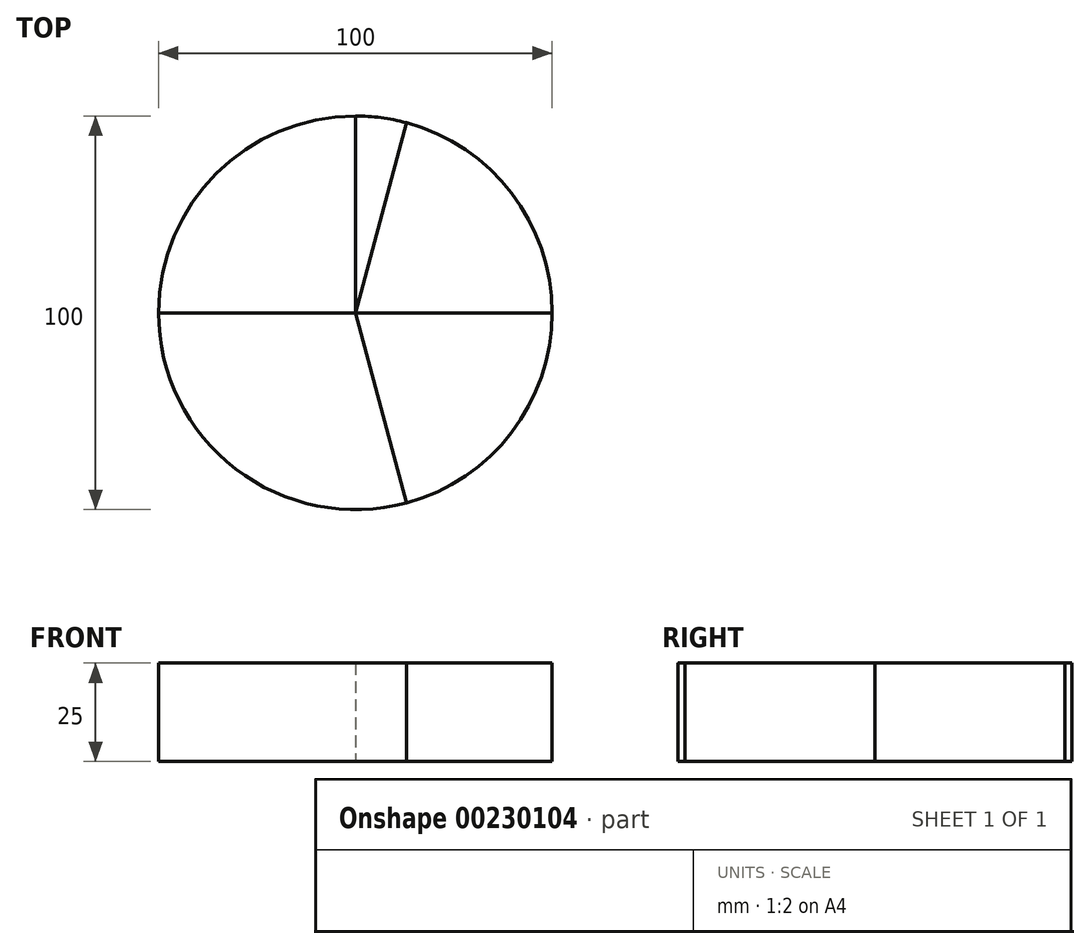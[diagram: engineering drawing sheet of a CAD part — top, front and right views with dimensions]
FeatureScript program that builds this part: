
annotation { "Feature Type Name" : "Feature", "Feature Type Description" : "" }
export const myFeature = defineFeature(function(context is Context, id is Id, definition is map)
    precondition{}
    {
        {
            var Q0;
            Q0=qCreatedBy(makeId("Top.planeOp"),FACE);
            var sketch = newSketch(context, id + "F0", { "sketchPlane" : qUnion([Q0])});
            skCircle(sketch, "E0", {"center": v(0, 0) * mm, "radius": 50 * mm});
            skLineSegment(sketch, "E1", {"start": v(0, 0) * mm, "end": v(12.94, 48.3) * mm});
            skLineSegment(sketch, "E2", {"start": v(0, 0) * mm, "end": v(-50, 0) * mm});
            skLineSegment(sketch, "E3", {"start": v(0, 0) * mm, "end": v(12.94, -48.3) * mm});
            skLineSegment(sketch, "E4", {"start": v(0, 0) * mm, "end": v(50, 0) * mm});
            skLineSegment(sketch, "E5", {"start": v(0, 0) * mm, "end": v(0, 50) * mm});
            skSolve(sketch);
        }
        {
            var Q0;
            {var subQ0=sQuery(id+"F0.wireOp",EDGE,"E1");Q0=makeQuery(id+"F0.imprint","IMPRINT",FACE,{"disambiguationData":[TD([[makeQuery(id+"F0.imprint","IMPRINT",EDGE,{"derivedFrom":subQ0}),1.0]])]});}
            var Q1;
            {var subQ0=sQuery(id+"F0.wireOp",EDGE,"E3");Q1=makeQuery(id+"F0.imprint","IMPRINT",FACE,{"disambiguationData":[TD([[makeQuery(id+"F0.imprint","IMPRINT",EDGE,{"derivedFrom":subQ0}),1.0]])]});}
            extrude(context, id + "F1", {"entities" : qUnion([Q0, Q1]), "depth" : 25 * mm});
        }
        {
            var Q0;
            {var subQ0=sQuery(id+"F0.wireOp",EDGE,"E1");Q0=makeQuery(id+"F0.imprint","IMPRINT",FACE,{"disambiguationData":[TD([[makeQuery(id+"F0.imprint","IMPRINT",EDGE,{"derivedFrom":subQ0}),-1.0]])]});}
            var Q1;
            {var subQ0=sQuery(id+"F0.wireOp",EDGE,"E2");Q1=makeQuery(id+"F0.imprint","IMPRINT",FACE,{"disambiguationData":[TD([[makeQuery(id+"F0.imprint","IMPRINT",EDGE,{"derivedFrom":subQ0}),1.0]])]});}
            extrude(context, id + "F2", {"entities" : qUnion([Q0, Q1]), "depth" : 25 * mm});
        }
        {
            var Q0;
            {var subQ0=sQuery(id+"F0.wireOp",EDGE,"E2");Q0=makeQuery(id+"F0.imprint","IMPRINT",FACE,{"disambiguationData":[TD([[makeQuery(id+"F0.imprint","IMPRINT",EDGE,{"derivedFrom":subQ0}),-1.0]])]});}
            extrude(context, id + "F3", {"entities" : qUnion([Q0]), "depth" : 25 * mm});
        }
    });
